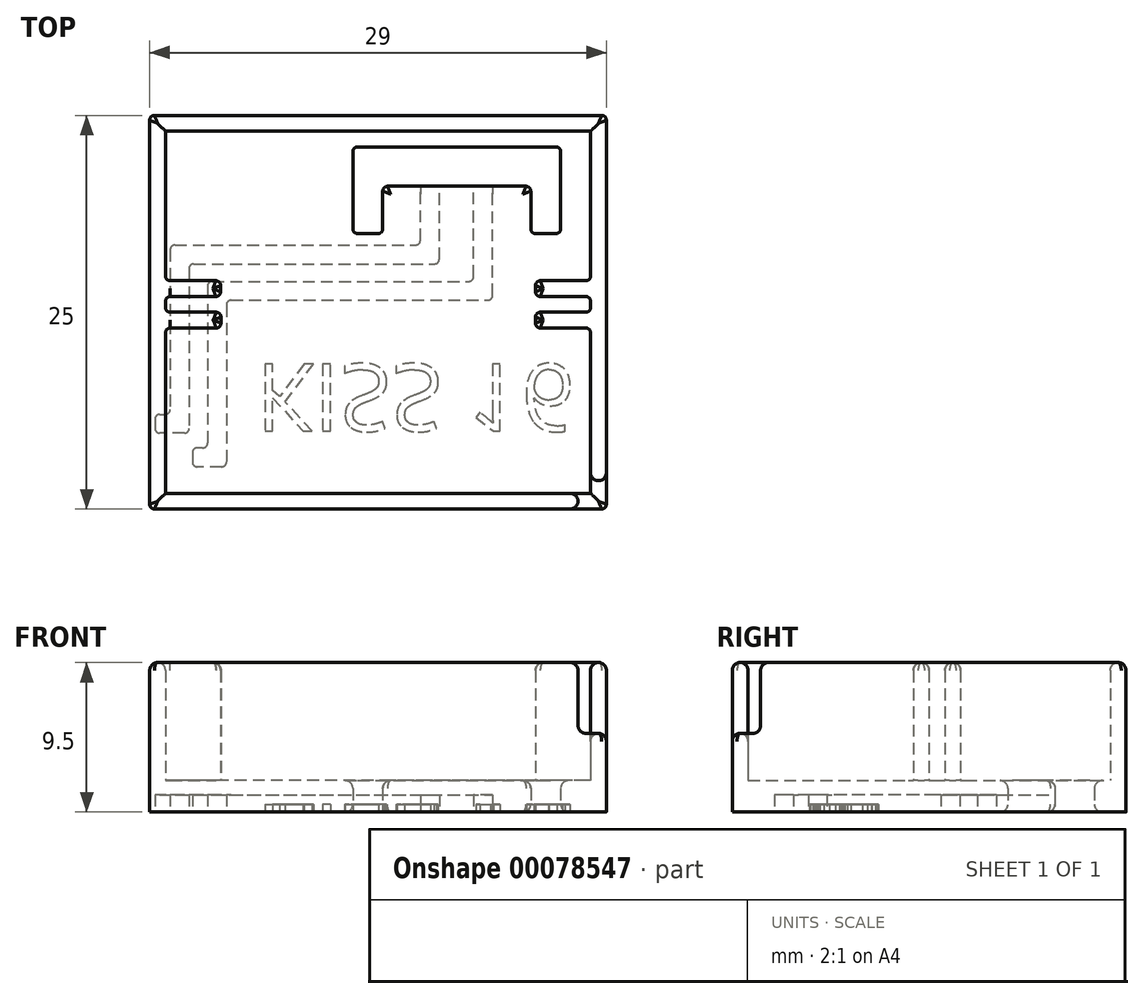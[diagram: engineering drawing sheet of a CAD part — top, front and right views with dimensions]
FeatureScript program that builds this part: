
annotation { "Feature Type Name" : "Feature", "Feature Type Description" : "" }
export const myFeature = defineFeature(function(context is Context, id is Id, definition is map)
    precondition{}
    {
        {
            var Q0;
            Q0=qCreatedBy(makeId("Top.planeOp"),FACE);
            var sketch = newSketch(context, id + "F0", { "sketchPlane" : qUnion([Q0])});
            skLineSegment(sketch, "E0.bottom", {"start": v(-16.18, 18.8) * mm, "end": v(10.82, 18.8) * mm});
            skLineSegment(sketch, "E0.top", {"start": v(-16.18, -4.2) * mm, "end": v(10.82, -4.2) * mm});
            skLineSegment(sketch, "E0.left", {"start": v(-16.18, 18.8) * mm, "end": v(-16.18, 9.6) * mm});
            skLineSegment(sketch, "E0.right", {"start": v(10.82, 18.8) * mm, "end": v(10.82, 9.6) * mm});
            skLineSegment(sketch, "E1.0", {"start": v(-16.88, 19.8) * mm, "end": v(11.52, 19.8) * mm});
            skLineSegment(sketch, "E1.1", {"start": v(-17.18, 19.5) * mm, "end": v(-17.18, -4.9) * mm});
            skLineSegment(sketch, "E1.2", {"start": v(-16.88, -5.2) * mm, "end": v(11.52, -5.2) * mm});
            skLineSegment(sketch, "E1.3", {"start": v(11.82, 19.5) * mm, "end": v(11.82, -4.9) * mm});
            skLineSegment(sketch, "E2", {"start": v(-15.88, 7.3) * mm, "end": v(-12.96, 7.3) * mm});
            skLineSegment(sketch, "E3.0", {"start": v(-15.88, 6.3) * mm, "end": v(-12.96, 6.3) * mm});
            skLineSegment(sketch, "E4.0", {"start": v(-15.88, 8.3) * mm, "end": v(-12.98, 8.3) * mm});
            skLineSegment(sketch, "E5.0", {"start": v(-15.88, 9.3) * mm, "end": v(-12.98, 9.3) * mm});
            skLineSegment(sketch, "E6", {"start": v(7.32, 9) * mm, "end": v(7.32, 8.6) * mm});
            skLineSegment(sketch, "E7", {"start": v(-12.68, 9) * mm, "end": v(-12.68, 8.6) * mm});
            skLineSegment(sketch, "E8.trimOffspring", {"start": v(7.62, 9.3) * mm, "end": v(10.52, 9.3) * mm});
            skLineSegment(sketch, "E9.trimOffspring", {"start": v(7.62, 8.3) * mm, "end": v(10.52, 8.3) * mm});
            skLineSegment(sketch, "E10.trimOffspring", {"start": v(7.62, 7.3) * mm, "end": v(10.52, 7.3) * mm});
            skLineSegment(sketch, "E11.trimOffspring", {"start": v(7.62, 6.3) * mm, "end": v(10.52, 6.3) * mm});
            skLineSegment(sketch, "E12", {"start": v(-12.66, 7) * mm, "end": v(-12.66, 6.6) * mm});
            skPoint(sketch, "E13.visualSharp", {"position": v(-12.68, 9.3) * mm});
            skArc(sketch, "E13.filletArc", {"start": v(-12.68, 9) * mm, "mid": v(-12.77, 9.21) * mm, "end": v(-12.98, 9.3) * mm});
            skArc(sketch, "E14.filletArc", {"start": v(-12.98, 8.3) * mm, "mid": v(-12.77, 8.39) * mm, "end": v(-12.68, 8.6) * mm});
            skArc(sketch, "E15.filletArc", {"start": v(-12.66, 7) * mm, "mid": v(-12.75, 7.21) * mm, "end": v(-12.96, 7.3) * mm});
            skPoint(sketch, "E16.visualSharp", {"position": v(-12.66, 6.3) * mm});
            skArc(sketch, "E16.filletArc", {"start": v(-12.96, 6.3) * mm, "mid": v(-12.75, 6.39) * mm, "end": v(-12.66, 6.6) * mm});
            skLineSegment(sketch, "E17", {"start": v(-16.18, 8) * mm, "end": v(-16.18, 7.6) * mm});
            skLineSegment(sketch, "E18", {"start": v(-16.18, 6) * mm, "end": v(-16.18, -4.2) * mm});
            skArc(sketch, "E19.filletArc", {"start": v(-16.18, 9.6) * mm, "mid": v(-16.1, 9.39) * mm, "end": v(-15.88, 9.3) * mm});
            skArc(sketch, "E20.filletArc", {"start": v(-15.88, 8.3) * mm, "mid": v(-16.1, 8.21) * mm, "end": v(-16.18, 8) * mm});
            skArc(sketch, "E21.filletArc", {"start": v(-16.18, 7.6) * mm, "mid": v(-16.1, 7.39) * mm, "end": v(-15.88, 7.3) * mm});
            skArc(sketch, "E22.filletArc", {"start": v(-15.88, 6.3) * mm, "mid": v(-16.1, 6.21) * mm, "end": v(-16.18, 6) * mm});
            skLineSegment(sketch, "E23", {"start": v(7.32, 7) * mm, "end": v(7.32, 6.6) * mm});
            skLineSegment(sketch, "E24", {"start": v(10.82, 8) * mm, "end": v(10.82, 7.6) * mm});
            skLineSegment(sketch, "E25", {"start": v(10.82, 6) * mm, "end": v(10.82, -4.2) * mm});
            skPoint(sketch, "E26.visualSharp", {"position": v(7.32, 9.3) * mm});
            skArc(sketch, "E26.filletArc", {"start": v(7.62, 9.3) * mm, "mid": v(7.4, 9.21) * mm, "end": v(7.32, 9) * mm});
            skArc(sketch, "E27.filletArc", {"start": v(7.32, 8.6) * mm, "mid": v(7.4, 8.39) * mm, "end": v(7.62, 8.3) * mm});
            skArc(sketch, "E28.filletArc", {"start": v(10.52, 9.3) * mm, "mid": v(10.73, 9.39) * mm, "end": v(10.82, 9.6) * mm});
            skArc(sketch, "E29.filletArc", {"start": v(10.82, 8) * mm, "mid": v(10.73, 8.21) * mm, "end": v(10.52, 8.3) * mm});
            skArc(sketch, "E30.filletArc", {"start": v(10.52, 7.3) * mm, "mid": v(10.73, 7.39) * mm, "end": v(10.82, 7.6) * mm});
            skArc(sketch, "E31.filletArc", {"start": v(7.62, 7.3) * mm, "mid": v(7.4, 7.21) * mm, "end": v(7.32, 7) * mm});
            skPoint(sketch, "E32.visualSharp", {"position": v(7.32, 6.3) * mm});
            skArc(sketch, "E32.filletArc", {"start": v(7.32, 6.6) * mm, "mid": v(7.4, 6.39) * mm, "end": v(7.62, 6.3) * mm});
            skArc(sketch, "E33.filletArc", {"start": v(10.82, 6) * mm, "mid": v(10.73, 6.21) * mm, "end": v(10.52, 6.3) * mm});
            skLineSegment(sketch, "E34.trimOffspring", {"start": v(10.82, -3.4) * mm, "end": v(11.82, -3.4) * mm});
            skLineSegment(sketch, "E35.trimOffspring", {"start": v(10.02, -4.2) * mm, "end": v(10.02, -5.2) * mm});
            skPoint(sketch, "E36.visualSharp", {"position": v(-17.18, 19.8) * mm});
            skArc(sketch, "E36.filletArc", {"start": v(-16.88, 19.8) * mm, "mid": v(-17.1, 19.71) * mm, "end": v(-17.18, 19.5) * mm});
            skPoint(sketch, "E37.visualSharp", {"position": v(11.82, 19.8) * mm});
            skArc(sketch, "E37.filletArc", {"start": v(11.82, 19.5) * mm, "mid": v(11.73, 19.71) * mm, "end": v(11.52, 19.8) * mm});
            skPoint(sketch, "E38.visualSharp", {"position": v(11.82, -5.2) * mm});
            skArc(sketch, "E38.filletArc", {"start": v(11.52, -5.2) * mm, "mid": v(11.73, -5.11) * mm, "end": v(11.82, -4.9) * mm});
            skPoint(sketch, "E39.visualSharp", {"position": v(-17.18, -5.2) * mm});
            skArc(sketch, "E39.filletArc", {"start": v(-17.18, -4.9) * mm, "mid": v(-17.1, -5.11) * mm, "end": v(-16.88, -5.2) * mm});
            skLineSegment(sketch, "E40", {"start": v(-3.98, 12.3) * mm, "end": v(-2.68, 12.3) * mm});
            skLineSegment(sketch, "E41", {"start": v(-3.98, 17.8) * mm, "end": v(8.62, 17.8) * mm});
            skLineSegment(sketch, "E42", {"start": v(2.32, 7.84) * mm, "end": v(2.32, 17.8) * mm, "construction": true});
            skLineSegment(sketch, "E43", {"start": v(-4.28, 17.5) * mm, "end": v(-4.28, 12.6) * mm});
            skLineSegment(sketch, "E44", {"start": v(-2.38, 15) * mm, "end": v(-2.38, 12.6) * mm});
            skLineSegment(sketch, "E45", {"start": v(-2.08, 15.3) * mm, "end": v(2.32, 15.3) * mm});
            skArc(sketch, "E46.filletArc", {"start": v(-4.28, 12.6) * mm, "mid": v(-4.2, 12.39) * mm, "end": v(-3.98, 12.3) * mm});
            skArc(sketch, "E47.filletArc", {"start": v(-3.98, 17.8) * mm, "mid": v(-4.2, 17.71) * mm, "end": v(-4.28, 17.5) * mm});
            skArc(sketch, "E48.filletArc", {"start": v(-2.08, 15.3) * mm, "mid": v(-2.3, 15.21) * mm, "end": v(-2.38, 15) * mm});
            skArc(sketch, "E49.MirrorCS", {"start": v(8.62, 17.8) * mm, "mid": v(8.83, 17.71) * mm, "end": v(8.92, 17.5) * mm});
            skArc(sketch, "E50.MirrorCS", {"start": v(8.92, 12.6) * mm, "mid": v(8.83, 12.39) * mm, "end": v(8.62, 12.3) * mm});
            skArc(sketch, "E51.MirrorCS", {"start": v(6.72, 15.3) * mm, "mid": v(6.93, 15.21) * mm, "end": v(7.02, 15) * mm});
            skLineSegment(sketch, "E52.MirrorCS", {"start": v(7.02, 15) * mm, "end": v(7.02, 12.6) * mm});
            skLineSegment(sketch, "E53.MirrorCS", {"start": v(8.92, 17.5) * mm, "end": v(8.92, 12.6) * mm});
            skLineSegment(sketch, "E54.MirrorCS", {"start": v(8.62, 12.3) * mm, "end": v(7.32, 12.3) * mm});
            skLineSegment(sketch, "E55.MirrorCS", {"start": v(6.72, 15.3) * mm, "end": v(2.32, 15.3) * mm});
            skPoint(sketch, "E56.visualSharp", {"position": v(-2.38, 12.3) * mm});
            skArc(sketch, "E56.filletArc", {"start": v(-2.68, 12.3) * mm, "mid": v(-2.47, 12.39) * mm, "end": v(-2.38, 12.6) * mm});
            skPoint(sketch, "E57.visualSharp", {"position": v(7.02, 12.3) * mm});
            skArc(sketch, "E57.filletArc", {"start": v(7.02, 12.6) * mm, "mid": v(7.1, 12.39) * mm, "end": v(7.32, 12.3) * mm});
            skLineSegment(sketch, "E58", {"start": v(-15.58, 11.57) * mm, "end": v(-0.3, 11.57) * mm});
            skLineSegment(sketch, "E59", {"start": v(-15.88, 11.27) * mm, "end": v(-15.88, 1.12) * mm});
            skLineSegment(sketch, "E60", {"start": v(-16.18, 0.82) * mm, "end": v(-16.55, 0.82) * mm});
            skLineSegment(sketch, "E61", {"start": v(0, 11.87) * mm, "end": v(0, 15.3) * mm});
            skArc(sketch, "E62.filletArc", {"start": v(-0.3, 11.57) * mm, "mid": v(-0.08, 11.66) * mm, "end": v(0, 11.87) * mm});
            skPoint(sketch, "E63.visualSharp", {"position": v(-15.88, 0.82) * mm});
            skArc(sketch, "E63.filletArc", {"start": v(-16.18, 0.82) * mm, "mid": v(-15.97, 0.9) * mm, "end": v(-15.88, 1.12) * mm});
            skArc(sketch, "E64.filletArc", {"start": v(-15.58, 11.57) * mm, "mid": v(-15.8, 11.48) * mm, "end": v(-15.88, 11.27) * mm});
            skLineSegment(sketch, "E65.0", {"start": v(1.2, 10.67) * mm, "end": v(1.2, 15.3) * mm});
            skLineSegment(sketch, "E65.2", {"start": v(-14.98, -0.38) * mm, "end": v(-16.55, -0.38) * mm});
            skLineSegment(sketch, "E65.4", {"start": v(-14.68, 10.07) * mm, "end": v(-14.68, -0.08) * mm});
            skLineSegment(sketch, "E65.5", {"start": v(-14.38, 10.37) * mm, "end": v(0.9, 10.37) * mm});
            skPoint(sketch, "E66.visualSharp", {"position": v(-14.68, 10.37) * mm});
            skArc(sketch, "E66.filletArc", {"start": v(-14.38, 10.37) * mm, "mid": v(-14.6, 10.28) * mm, "end": v(-14.68, 10.07) * mm});
            skArc(sketch, "E67.filletArc", {"start": v(0.9, 10.37) * mm, "mid": v(1.12, 10.46) * mm, "end": v(1.2, 10.67) * mm});
            skArc(sketch, "E68.filletArc", {"start": v(-14.98, -0.38) * mm, "mid": v(-14.77, -0.3) * mm, "end": v(-14.68, -0.08) * mm});
            skLineSegment(sketch, "E69", {"start": v(-16.85, 0.52) * mm, "end": v(-16.85, -0.08) * mm});
            skArc(sketch, "E70.filletArc", {"start": v(-16.55, 0.82) * mm, "mid": v(-16.76, 0.73) * mm, "end": v(-16.85, 0.52) * mm});
            skArc(sketch, "E71.filletArc", {"start": v(-16.85, -0.08) * mm, "mid": v(-16.76, -0.3) * mm, "end": v(-16.55, -0.38) * mm});
            skLineSegment(sketch, "E72", {"start": v(-13.21, 9.26) * mm, "end": v(3.09, 9.26) * mm});
            skLineSegment(sketch, "E73", {"start": v(-13.51, 8.96) * mm, "end": v(-13.51, -1.02) * mm});
            skLineSegment(sketch, "E74", {"start": v(-13.81, -1.32) * mm, "end": v(-14.17, -1.32) * mm});
            skLineSegment(sketch, "E75", {"start": v(3.39, 9.56) * mm, "end": v(3.39, 15.3) * mm});
            skArc(sketch, "E76.filletArc", {"start": v(3.09, 9.26) * mm, "mid": v(3.3, 9.35) * mm, "end": v(3.39, 9.56) * mm});
            skPoint(sketch, "E77.visualSharp", {"position": v(-13.51, -1.32) * mm});
            skArc(sketch, "E77.filletArc", {"start": v(-13.81, -1.32) * mm, "mid": v(-13.6, -1.23) * mm, "end": v(-13.51, -1.02) * mm});
            skArc(sketch, "E78.filletArc", {"start": v(-13.21, 9.26) * mm, "mid": v(-13.42, 9.17) * mm, "end": v(-13.51, 8.96) * mm});
            skLineSegment(sketch, "E79.0", {"start": v(4.59, 8.36) * mm, "end": v(4.59, 15.3) * mm});
            skLineSegment(sketch, "E79.2", {"start": v(-12.61, -2.52) * mm, "end": v(-14.17, -2.52) * mm});
            skLineSegment(sketch, "E79.4", {"start": v(-12.31, 7.76) * mm, "end": v(-12.31, -2.22) * mm});
            skLineSegment(sketch, "E79.5", {"start": v(-12.01, 8.06) * mm, "end": v(4.29, 8.06) * mm});
            skArc(sketch, "E80.filletArc", {"start": v(-12.01, 8.06) * mm, "mid": v(-12.22, 7.97) * mm, "end": v(-12.31, 7.76) * mm});
            skArc(sketch, "E81.filletArc", {"start": v(4.29, 8.06) * mm, "mid": v(4.5, 8.15) * mm, "end": v(4.59, 8.36) * mm});
            skArc(sketch, "E82.filletArc", {"start": v(-12.61, -2.52) * mm, "mid": v(-12.4, -2.43) * mm, "end": v(-12.31, -2.22) * mm});
            skLineSegment(sketch, "E83", {"start": v(-14.47, -1.62) * mm, "end": v(-14.47, -2.22) * mm});
            skArc(sketch, "E84.filletArc", {"start": v(-14.17, -1.32) * mm, "mid": v(-14.39, -1.4) * mm, "end": v(-14.47, -1.62) * mm});
            skArc(sketch, "E85.filletArc", {"start": v(-14.47, -2.22) * mm, "mid": v(-14.39, -2.43) * mm, "end": v(-14.17, -2.52) * mm});
            skPoint(sketch, "E86.orphan", {"position": v(2.32, 17.8) * mm});
            skSolve(sketch);
        }
        {
            var Q0;
            {var subQ0=sQuery(id+"F0.wireOp",EDGE,"E20.filletArc");var subQ1=sQuery(id+"F0.wireOp",EDGE,"E4.0");var subQ2=makeQuery(id+"F0.imprint","INTERSECT",VERTEX,{"derivedFrom":[subQ1,subQ0]});Q0=makeQuery(id+"F0.imprint","IMPRINT",FACE,{"disambiguationData":[TD([[makeQuery(id+"F0.imprint","IMPRINT",EDGE,{"disambiguationData":[TD([[subQ2,-1.0]])],"derivedFrom":subQ1}),1.0]])]});}
            var Q1;
            {var subQ0=sQuery(id+"F0.wireOp",EDGE,"E65.4");var subQ1=sQuery(id+"F0.wireOp",EDGE,"E4.0");var subQ2=makeQuery(id+"F0.imprint","INTERSECT",VERTEX,{"derivedFrom":[subQ1,subQ0]});Q1=makeQuery(id+"F0.imprint","IMPRINT",FACE,{"disambiguationData":[TD([[makeQuery(id+"F0.imprint","IMPRINT",EDGE,{"disambiguationData":[TD([[subQ2,-1.0]])],"derivedFrom":subQ1}),1.0]])]});}
            var Q2;
            {var subQ3=sQuery(id+"F0.wireOp",EDGE,"E34.trimOffspring");Q2=makeQuery(id+"F0.imprint","IMPRINT",FACE,{"disambiguationData":[TD([[makeQuery(id+"F0.imprint","IMPRINT",EDGE,{"derivedFrom":subQ3}),-1.0]])]});}
            var Q3;
            Q3=makeQuery(id+"F0.imprint","IMPRINT",FACE,{"disambiguationData":[TD([[makeQuery(id+"F0.imprint","IMPRINT",EDGE,{"derivedFrom":sQuery(id+"F0.wireOp",EDGE,"E7")}),-1.0]])]});
            var Q4;
            Q4=makeQuery(id+"F0.imprint","IMPRINT",FACE,{"disambiguationData":[TD([[makeQuery(id+"F0.imprint","IMPRINT",EDGE,{"derivedFrom":sQuery(id+"F0.wireOp",EDGE,"E0.bottom")}),1.0]])]});
            var Q5;
            Q5=makeQuery(id+"F0.imprint","IMPRINT",FACE,{"disambiguationData":[TD([[makeQuery(id+"F0.imprint","IMPRINT",EDGE,{"derivedFrom":sQuery(id+"F0.wireOp",EDGE,"E7")}),1.0]])]});
            var Q6;
            {var subQ11=sQuery(id+"F0.wireOp",EDGE,"E65.0");Q6=makeQuery(id+"F0.imprint","IMPRINT",FACE,{"disambiguationData":[TD([[makeQuery(id+"F0.imprint","IMPRINT",EDGE,{"derivedFrom":subQ11}),-1.0]])]});}
            var Q7;
            Q7=makeQuery(id+"F0.imprint","IMPRINT",FACE,{"disambiguationData":[TD([[makeQuery(id+"F0.imprint","IMPRINT",EDGE,{"derivedFrom":sQuery(id+"F0.wireOp",EDGE,"E58")}),-1.0]])]});
            var Q8;
            Q8=makeQuery(id+"F0.imprint","IMPRINT",FACE,{"disambiguationData":[TD([[makeQuery(id+"F0.imprint","IMPRINT",EDGE,{"derivedFrom":sQuery(id+"F0.wireOp",EDGE,"E0.bottom")}),-1.0]])]});
            var Q9;
            {var subQ0=sQuery(id+"F0.wireOp",EDGE,"E21.filletArc");var subQ1=sQuery(id+"F0.wireOp",EDGE,"E2");var subQ2=makeQuery(id+"F0.imprint","INTERSECT",VERTEX,{"derivedFrom":[subQ1,subQ0]});Q9=makeQuery(id+"F0.imprint","IMPRINT",FACE,{"disambiguationData":[TD([[makeQuery(id+"F0.imprint","IMPRINT",EDGE,{"disambiguationData":[TD([[subQ2,-1.0]])],"derivedFrom":subQ1}),1.0]])]});}
            var Q10;
            {var subQ0=sQuery(id+"F0.wireOp",EDGE,"E22.filletArc");var subQ1=sQuery(id+"F0.wireOp",EDGE,"E18");var subQ2=makeQuery(id+"F0.imprint","INTERSECT",VERTEX,{"derivedFrom":[subQ1,subQ0]});Q10=makeQuery(id+"F0.imprint","IMPRINT",FACE,{"disambiguationData":[TD([[makeQuery(id+"F0.imprint","IMPRINT",EDGE,{"disambiguationData":[TD([[subQ2,-1.0]])],"derivedFrom":subQ1}),1.0]])]});}
            var Q11;
            Q11=makeQuery(id+"F0.imprint","IMPRINT",FACE,{"disambiguationData":[TD([[makeQuery(id+"F0.imprint","IMPRINT",EDGE,{"derivedFrom":sQuery(id+"F0.wireOp",EDGE,"E12")}),-1.0]])]});
            var Q12;
            {var subQ9=sQuery(id+"F0.wireOp",EDGE,"E68.filletArc");Q12=makeQuery(id+"F0.imprint","IMPRINT",FACE,{"disambiguationData":[TD([[makeQuery(id+"F0.imprint","IMPRINT",EDGE,{"derivedFrom":subQ9}),1.0]])]});}
            var Q13;
            {var subQ0=sQuery(id+"F0.wireOp",EDGE,"E65.4");var subQ1=sQuery(id+"F0.wireOp",EDGE,"E2");var subQ2=makeQuery(id+"F0.imprint","INTERSECT",VERTEX,{"derivedFrom":[subQ1,subQ0]});Q13=makeQuery(id+"F0.imprint","IMPRINT",FACE,{"disambiguationData":[TD([[makeQuery(id+"F0.imprint","IMPRINT",EDGE,{"disambiguationData":[TD([[subQ2,-1.0]])],"derivedFrom":subQ1}),1.0]])]});}
            var Q14;
            {var subQ0=sQuery(id+"F0.wireOp",EDGE,"E65.4");var subQ1=sQuery(id+"F0.wireOp",EDGE,"E2");var subQ2=makeQuery(id+"F0.imprint","INTERSECT",VERTEX,{"derivedFrom":[subQ1,subQ0]});Q14=makeQuery(id+"F0.imprint","IMPRINT",FACE,{"disambiguationData":[TD([[makeQuery(id+"F0.imprint","IMPRINT",EDGE,{"disambiguationData":[TD([[subQ2,-1.0]])],"derivedFrom":subQ1}),-1.0]])]});}
            var Q15;
            {var subQ5=sQuery(id+"F0.wireOp",EDGE,"E21.filletArc");var subQ6=sQuery(id+"F0.wireOp",EDGE,"E2");var subQ7=makeQuery(id+"F0.imprint","INTERSECT",VERTEX,{"derivedFrom":[subQ6,subQ5]});Q15=makeQuery(id+"F0.imprint","IMPRINT",FACE,{"disambiguationData":[TD([[makeQuery(id+"F0.imprint","IMPRINT",EDGE,{"disambiguationData":[TD([[subQ7,-1.0]])],"derivedFrom":subQ6}),-1.0]])]});}
            var Q16;
            {var subQ6=sQuery(id+"F0.wireOp",EDGE,"E60");Q16=makeQuery(id+"F0.imprint","IMPRINT",FACE,{"disambiguationData":[TD([[makeQuery(id+"F0.imprint","IMPRINT",EDGE,{"derivedFrom":subQ6}),1.0]])]});}
            var Q17;
            {var subQ0=sQuery(id+"F0.wireOp",EDGE,"E17");Q17=makeQuery(id+"F0.imprint","IMPRINT",FACE,{"disambiguationData":[TD([[makeQuery(id+"F0.imprint","IMPRINT",EDGE,{"derivedFrom":subQ0}),1.0]])]});}
            extrude(context, id + "F1", {"entities" : qUnion([Q0, Q1, Q2, Q3, Q4, Q5, Q6, Q7, Q8, Q9, Q10, Q11, Q12, Q13, Q14, Q15, Q16, Q17]), "depth" : 2 * mm});
        }
        {
            var Q0;
            Q0=makeQuery(id+"F0.imprint","IMPRINT",FACE,{"disambiguationData":[TD([[makeQuery(id+"F0.imprint","IMPRINT",EDGE,{"derivedFrom":sQuery(id+"F0.wireOp",EDGE,"E0.bottom")}),1.0]])]});
            var Q1;
            {var subQ6=sQuery(id+"F0.wireOp",EDGE,"E60");Q1=makeQuery(id+"F0.imprint","IMPRINT",FACE,{"disambiguationData":[TD([[makeQuery(id+"F0.imprint","IMPRINT",EDGE,{"derivedFrom":subQ6}),1.0]])]});}
            var Q2;
            {var subQ0=sQuery(id+"F0.wireOp",EDGE,"E20.filletArc");var subQ1=sQuery(id+"F0.wireOp",EDGE,"E4.0");var subQ2=makeQuery(id+"F0.imprint","INTERSECT",VERTEX,{"derivedFrom":[subQ1,subQ0]});Q2=makeQuery(id+"F0.imprint","IMPRINT",FACE,{"disambiguationData":[TD([[makeQuery(id+"F0.imprint","IMPRINT",EDGE,{"disambiguationData":[TD([[subQ2,-1.0]])],"derivedFrom":subQ1}),1.0]])]});}
            var Q3;
            {var subQ5=sQuery(id+"F0.wireOp",EDGE,"E21.filletArc");var subQ6=sQuery(id+"F0.wireOp",EDGE,"E2");var subQ7=makeQuery(id+"F0.imprint","INTERSECT",VERTEX,{"derivedFrom":[subQ6,subQ5]});Q3=makeQuery(id+"F0.imprint","IMPRINT",FACE,{"disambiguationData":[TD([[makeQuery(id+"F0.imprint","IMPRINT",EDGE,{"disambiguationData":[TD([[subQ7,-1.0]])],"derivedFrom":subQ6}),-1.0]])]});}
            var Q4;
            {var subQ0=sQuery(id+"F0.wireOp",EDGE,"E65.4");var subQ1=sQuery(id+"F0.wireOp",EDGE,"E2");var subQ2=makeQuery(id+"F0.imprint","INTERSECT",VERTEX,{"derivedFrom":[subQ1,subQ0]});Q4=makeQuery(id+"F0.imprint","IMPRINT",FACE,{"disambiguationData":[TD([[makeQuery(id+"F0.imprint","IMPRINT",EDGE,{"disambiguationData":[TD([[subQ2,-1.0]])],"derivedFrom":subQ1}),-1.0]])]});}
            var Q5;
            {var subQ0=sQuery(id+"F0.wireOp",EDGE,"E65.4");var subQ1=sQuery(id+"F0.wireOp",EDGE,"E4.0");var subQ2=makeQuery(id+"F0.imprint","INTERSECT",VERTEX,{"derivedFrom":[subQ1,subQ0]});Q5=makeQuery(id+"F0.imprint","IMPRINT",FACE,{"disambiguationData":[TD([[makeQuery(id+"F0.imprint","IMPRINT",EDGE,{"disambiguationData":[TD([[subQ2,-1.0]])],"derivedFrom":subQ1}),1.0]])]});}
            var Q6;
            Q6=makeQuery(id+"F0.imprint","IMPRINT",FACE,{"disambiguationData":[TD([[makeQuery(id+"F0.imprint","IMPRINT",EDGE,{"derivedFrom":sQuery(id+"F0.wireOp",EDGE,"E7")}),-1.0]])]});
            var Q7;
            Q7=makeQuery(id+"F0.imprint","IMPRINT",FACE,{"disambiguationData":[TD([[makeQuery(id+"F0.imprint","IMPRINT",EDGE,{"derivedFrom":sQuery(id+"F0.wireOp",EDGE,"E12")}),-1.0]])]});
            extrude(context, id + "F2", {"entities" : qUnion([Q0, Q1, Q2, Q3, Q4, Q5, Q6, Q7]), "operationType" : NewBodyOperationType.ADD, "depth" : 9.5 * mm});
        }
        {
            var Q0;
            {var subQ3=sQuery(id+"F0.wireOp",EDGE,"E34.trimOffspring");Q0=makeQuery(id+"F0.imprint","IMPRINT",FACE,{"disambiguationData":[TD([[makeQuery(id+"F0.imprint","IMPRINT",EDGE,{"derivedFrom":subQ3}),-1.0]])]});}
            extrude(context, id + "F3", {"entities" : qUnion([Q0]), "operationType" : NewBodyOperationType.ADD, "depth" : 5 * mm});
        }
        {
            var Q0;
            {var subQ9=sQuery(id+"F0.wireOp",EDGE,"E68.filletArc");Q0=makeQuery(id+"F0.imprint","IMPRINT",FACE,{"disambiguationData":[TD([[makeQuery(id+"F0.imprint","IMPRINT",EDGE,{"derivedFrom":subQ9}),1.0]])]});}
            var Q1;
            {var subQ5=sQuery(id+"F0.wireOp",EDGE,"E21.filletArc");var subQ6=sQuery(id+"F0.wireOp",EDGE,"E2");var subQ7=makeQuery(id+"F0.imprint","INTERSECT",VERTEX,{"derivedFrom":[subQ6,subQ5]});Q1=makeQuery(id+"F0.imprint","IMPRINT",FACE,{"disambiguationData":[TD([[makeQuery(id+"F0.imprint","IMPRINT",EDGE,{"disambiguationData":[TD([[subQ7,-1.0]])],"derivedFrom":subQ6}),-1.0]])]});}
            var Q2;
            {var subQ0=sQuery(id+"F0.wireOp",EDGE,"E21.filletArc");var subQ1=sQuery(id+"F0.wireOp",EDGE,"E2");var subQ2=makeQuery(id+"F0.imprint","INTERSECT",VERTEX,{"derivedFrom":[subQ1,subQ0]});Q2=makeQuery(id+"F0.imprint","IMPRINT",FACE,{"disambiguationData":[TD([[makeQuery(id+"F0.imprint","IMPRINT",EDGE,{"disambiguationData":[TD([[subQ2,-1.0]])],"derivedFrom":subQ1}),1.0]])]});}
            var Q3;
            {var subQ0=sQuery(id+"F0.wireOp",EDGE,"E20.filletArc");var subQ1=sQuery(id+"F0.wireOp",EDGE,"E4.0");var subQ2=makeQuery(id+"F0.imprint","INTERSECT",VERTEX,{"derivedFrom":[subQ1,subQ0]});Q3=makeQuery(id+"F0.imprint","IMPRINT",FACE,{"disambiguationData":[TD([[makeQuery(id+"F0.imprint","IMPRINT",EDGE,{"disambiguationData":[TD([[subQ2,-1.0]])],"derivedFrom":subQ1}),1.0]])]});}
            var Q4;
            Q4=makeQuery(id+"F0.imprint","IMPRINT",FACE,{"disambiguationData":[TD([[makeQuery(id+"F0.imprint","IMPRINT",EDGE,{"derivedFrom":sQuery(id+"F0.wireOp",EDGE,"E58")}),-1.0]])]});
            var Q5;
            {var subQ6=sQuery(id+"F0.wireOp",EDGE,"E60");Q5=makeQuery(id+"F0.imprint","IMPRINT",FACE,{"disambiguationData":[TD([[makeQuery(id+"F0.imprint","IMPRINT",EDGE,{"derivedFrom":subQ6}),1.0]])]});}
            var Q6;
            Q6=makeQuery(id+"F0.imprint","IMPRINT",FACE,{"disambiguationData":[TD([[makeQuery(id+"F0.imprint","IMPRINT",EDGE,{"derivedFrom":sQuery(id+"F0.wireOp",EDGE,"E7")}),1.0]])]});
            var Q7;
            Q7=makeQuery(id+"F0.imprint","IMPRINT",FACE,{"disambiguationData":[TD([[makeQuery(id+"F0.imprint","IMPRINT",EDGE,{"derivedFrom":sQuery(id+"F0.wireOp",EDGE,"E12")}),-1.0]])]});
            var Q8;
            Q8=makeQuery(id+"F0.imprint","IMPRINT",FACE,{"disambiguationData":[TD([[makeQuery(id+"F0.imprint","IMPRINT",EDGE,{"derivedFrom":sQuery(id+"F0.wireOp",EDGE,"E7")}),-1.0]])]});
            extrude(context, id + "F4", {"entities" : qUnion([Q0, Q1, Q2, Q3, Q4, Q5, Q6, Q7, Q8]), "operationType" : NewBodyOperationType.REMOVE, "depth" : 1.1 * mm});
        }
        {
            var Q0;
            Q0=makeQuery(id+"F1.opExtrude","CAP_FACE",FACE,{"disambiguationData":[OSD([sQuery(id+"F0.wireOp",EDGE,"E1.0"),sQuery(id+"F0.wireOp",EDGE,"E1.1"),sQuery(id+"F0.wireOp",EDGE,"E1.2"),sQuery(id+"F0.wireOp",EDGE,"E1.3"),sQuery(id+"F0.wireOp",EDGE,"E36.filletArc"),sQuery(id+"F0.wireOp",EDGE,"E37.filletArc"),sQuery(id+"F0.wireOp",EDGE,"E38.filletArc"),sQuery(id+"F0.wireOp",EDGE,"E39.filletArc"),sQuery(id+"F0.wireOp",EDGE,"E40"),sQuery(id+"F0.wireOp",EDGE,"E41"),sQuery(id+"F0.wireOp",EDGE,"E43"),sQuery(id+"F0.wireOp",EDGE,"E44"),sQuery(id+"F0.wireOp",EDGE,"E45"),sQuery(id+"F0.wireOp",EDGE,"E46.filletArc"),sQuery(id+"F0.wireOp",EDGE,"E47.filletArc"),sQuery(id+"F0.wireOp",EDGE,"E48.filletArc"),sQuery(id+"F0.wireOp",EDGE,"E49.MirrorCS"),sQuery(id+"F0.wireOp",EDGE,"E50.MirrorCS"),sQuery(id+"F0.wireOp",EDGE,"E51.MirrorCS"),sQuery(id+"F0.wireOp",EDGE,"E52.MirrorCS"),sQuery(id+"F0.wireOp",EDGE,"E53.MirrorCS"),sQuery(id+"F0.wireOp",EDGE,"E54.MirrorCS"),sQuery(id+"F0.wireOp",EDGE,"E55.MirrorCS"),sQuery(id+"F0.wireOp",EDGE,"E56.filletArc"),sQuery(id+"F0.wireOp",EDGE,"E57.filletArc")])],"isStart":true});
            var sketch = newSketch(context, id + "F5", { "sketchPlane" : qUnion([Q0])});
            skText(sketch, "E87", { "text": "KISS 16", "fontName": "OpenSans-Regular.ttf"});
            const initialGuessF5  = {"E87": [-0.01046, -0.00401, 1, 0, 0.0043]};
            skSetInitialGuess(sketch, initialGuessF5);
            skSolve(sketch);
        }
        {
            var Q0;
            Q0 = qSketchRegion(id + "F5", true);
            extrude(context, id + "F6", {"entities" : qUnion([Q0]), "operationType" : NewBodyOperationType.REMOVE, "oppositeDirection" : true, "depth" : 0.5 * mm});
        }
        {
            var Q0;
            Q0=makeQuery(id+"F2.opExtrude","CAP_FACE",FACE,{"disambiguationData":[OSD([sQuery(id+"F0.wireOp",EDGE,"E0.bottom"),sQuery(id+"F0.wireOp",EDGE,"E0.top"),sQuery(id+"F0.wireOp",EDGE,"E0.left"),sQuery(id+"F0.wireOp",EDGE,"E0.right"),sQuery(id+"F0.wireOp",EDGE,"E1.0"),sQuery(id+"F0.wireOp",EDGE,"E1.1"),sQuery(id+"F0.wireOp",EDGE,"E1.2"),sQuery(id+"F0.wireOp",EDGE,"E1.3"),sQuery(id+"F0.wireOp",EDGE,"E2"),sQuery(id+"F0.wireOp",EDGE,"E3.0"),sQuery(id+"F0.wireOp",EDGE,"E4.0"),sQuery(id+"F0.wireOp",EDGE,"E5.0"),sQuery(id+"F0.wireOp",EDGE,"E6"),sQuery(id+"F0.wireOp",EDGE,"E7"),sQuery(id+"F0.wireOp",EDGE,"E8.trimOffspring"),sQuery(id+"F0.wireOp",EDGE,"E9.trimOffspring"),sQuery(id+"F0.wireOp",EDGE,"E10.trimOffspring"),sQuery(id+"F0.wireOp",EDGE,"E11.trimOffspring"),sQuery(id+"F0.wireOp",EDGE,"E12"),sQuery(id+"F0.wireOp",EDGE,"E13.filletArc"),sQuery(id+"F0.wireOp",EDGE,"E14.filletArc"),sQuery(id+"F0.wireOp",EDGE,"E15.filletArc"),sQuery(id+"F0.wireOp",EDGE,"E16.filletArc"),sQuery(id+"F0.wireOp",EDGE,"E17"),sQuery(id+"F0.wireOp",EDGE,"E18"),sQuery(id+"F0.wireOp",EDGE,"E19.filletArc"),sQuery(id+"F0.wireOp",EDGE,"E20.filletArc"),sQuery(id+"F0.wireOp",EDGE,"E21.filletArc"),sQuery(id+"F0.wireOp",EDGE,"E22.filletArc"),sQuery(id+"F0.wireOp",EDGE,"E23"),sQuery(id+"F0.wireOp",EDGE,"E24"),sQuery(id+"F0.wireOp",EDGE,"E25"),sQuery(id+"F0.wireOp",EDGE,"E26.filletArc"),sQuery(id+"F0.wireOp",EDGE,"E27.filletArc"),sQuery(id+"F0.wireOp",EDGE,"E28.filletArc"),sQuery(id+"F0.wireOp",EDGE,"E29.filletArc"),sQuery(id+"F0.wireOp",EDGE,"E30.filletArc"),sQuery(id+"F0.wireOp",EDGE,"E31.filletArc"),sQuery(id+"F0.wireOp",EDGE,"E32.filletArc"),sQuery(id+"F0.wireOp",EDGE,"E33.filletArc"),sQuery(id+"F0.wireOp",EDGE,"E34.trimOffspring"),sQuery(id+"F0.wireOp",EDGE,"E35.trimOffspring"),sQuery(id+"F0.wireOp",EDGE,"E36.filletArc"),sQuery(id+"F0.wireOp",EDGE,"E37.filletArc"),sQuery(id+"F0.wireOp",EDGE,"E39.filletArc")])],"isStart":false});
            fillet(context, id + "F7", {"entities" : qUnion([Q0]), "radius" : 0.5 * mm, "tangentPropagation" : true, "allowEdgeOverflow" : false});
        }
        {
            var Q0;
            Q0=makeQuery(id+"F1.opExtrude","CAP_EDGE",EDGE,{"disambiguationData":[OSD([sQuery(id+"F0.wireOp",EDGE,"E53.MirrorCS")])],"isStart":false});
            var Q1;
            Q1=makeQuery(id+"F1.opExtrude","CAP_EDGE",EDGE,{"disambiguationData":[OSD([sQuery(id+"F0.wireOp",EDGE,"E41")])],"isStart":true});
            fillet(context, id + "F8", {"entities" : qUnion([Q0, Q1]), "radius" : 0.5 * mm, "tangentPropagation" : true, "allowEdgeOverflow" : false});
        }
        {
            var Q0;
            Q0=makeQuery(id+"F3.opExtrude","CAP_FACE",FACE,{"disambiguationData":[OSD([sQuery(id+"F0.wireOp",EDGE,"E0.top"),sQuery(id+"F0.wireOp",EDGE,"E1.2"),sQuery(id+"F0.wireOp",EDGE,"E1.3"),sQuery(id+"F0.wireOp",EDGE,"E25"),sQuery(id+"F0.wireOp",EDGE,"E34.trimOffspring"),sQuery(id+"F0.wireOp",EDGE,"E35.trimOffspring"),sQuery(id+"F0.wireOp",EDGE,"E38.filletArc")])],"isStart":false});
            var Q1;
            Q1=makeQuery(id+"F2.opExtrude","SWEPT_FACE",FACE,{"disambiguationData":[OSD([sQuery(id+"F0.wireOp",EDGE,"E34.trimOffspring")])]});
            var Q2;
            Q2=makeQuery(id+"F2.opExtrude","SWEPT_FACE",FACE,{"disambiguationData":[OSD([sQuery(id+"F0.wireOp",EDGE,"E35.trimOffspring")])]});
            fillet(context, id + "F9", {"entities" : qUnion([Q0, Q1, Q2]), "radius" : 0.5 * mm, "tangentPropagation" : true, "allowEdgeOverflow" : false});
        }
    });
